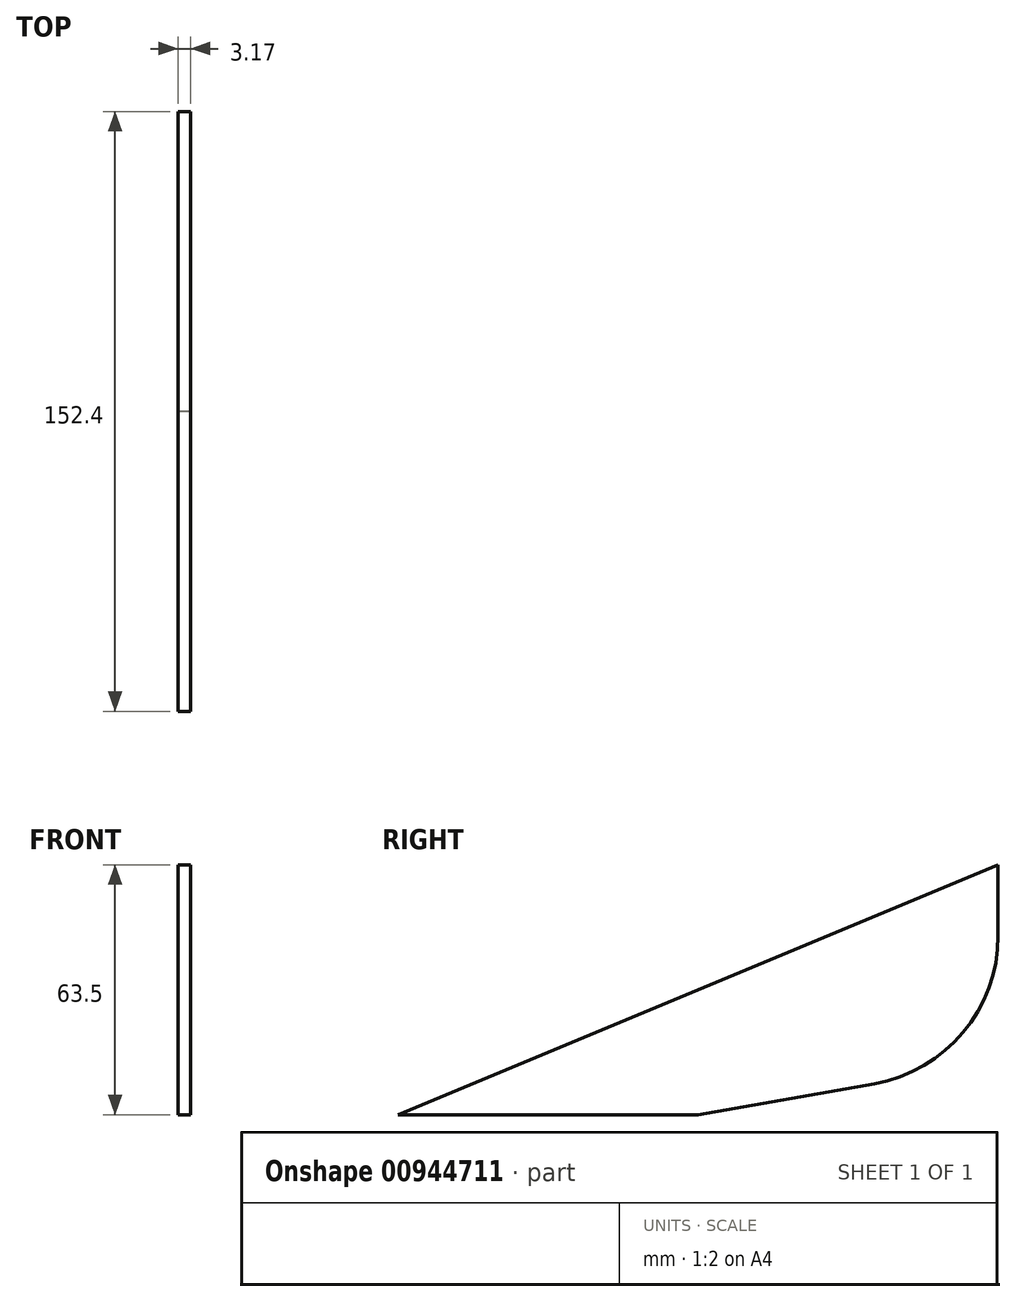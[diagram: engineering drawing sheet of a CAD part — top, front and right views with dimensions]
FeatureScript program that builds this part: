
annotation { "Feature Type Name" : "Feature", "Feature Type Description" : "" }
export const myFeature = defineFeature(function(context is Context, id is Id, definition is map)
    precondition{}
    {
        {
            var Q0;
            Q0=qCreatedBy(makeId("Right.planeOp"),FACE);
            var sketch = newSketch(context, id + "F0", { "sketchPlane" : qUnion([Q0])});
            skLineSegment(sketch, "E0.bottom", {"start": v(0, 0) * mm, "end": v(152.4, 0) * mm});
            skLineSegment(sketch, "E0.top", {"start": v(0, 63.5) * mm, "end": v(152.4, 63.5) * mm});
            skLineSegment(sketch, "E0.left", {"start": v(0, 0) * mm, "end": v(0, 63.5) * mm});
            skLineSegment(sketch, "E0.right", {"start": v(152.4, 45.4) * mm, "end": v(152.4, 63.5) * mm});
            skLineSegment(sketch, "E1", {"start": v(0, 0) * mm, "end": v(152.4, 63.5) * mm});
            skLineSegment(sketch, "E2", {"start": v(76.2, 0) * mm, "end": v(120.92, 7.88) * mm});
            skArc(sketch, "E3.filletArc", {"start": v(120.92, 7.88) * mm, "mid": v(143.49, 20.92) * mm, "end": v(152.4, 45.4) * mm});
            skSolve(sketch);
        }
        {
            var Q0;
            Q0=makeQuery(id+"F0.imprint","IMPRINT",FACE,{"disambiguationData":[TD([[makeQuery(id+"F0.imprint","IMPRINT",EDGE,{"derivedFrom":sQuery(id+"F0.wireOp",EDGE,"E0.right")}),1.0]])]});
            extrude(context, id + "F1", {"entities" : qUnion([Q0]), "depth" : 3.17 * mm, "offsetDistance" : 25.4 * mm});
        }
    });
